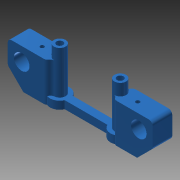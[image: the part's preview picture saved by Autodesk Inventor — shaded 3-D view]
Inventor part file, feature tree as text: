
AUTODESK INVENTOR PART (.ipt)
format: ipt  version: 2013 SP2 (Build 170200200, 200)  size: 180,736 bytes
history: native  units: mm
features: extrude x5, sketch x4, chamfer x1, fillet x1
ambient origin geometry x8: Origin, YZ Plane, XZ Plane, XY Plane, X Axis, Y Axis, Z Axis, Center Point
bodies: Solid1 (feature_tree)
feature tree (11):
  extrude  "Extrusion1"  Depth=6.0mm
  extrude  "Extrusion2"  Depth=10.0mm
  extrude  "Extrusion3"  Depth=4.0mm
  extrude  "Extrusion4"  Depth=20.0mm
  chamfer  "Chamfer1"  Distance=20.0mm
  fillet  "Fillet1"  Radius=8.0mm
  extrude  "Extrusion5"  Depth=8.0mm
  sketch  "Sketch2"  dims[d0=3.3mm d1=6.0mm]
  sketch  "Sketch3"  dims[d2=26.0mm d3=0.0mm d4=10.0mm]
  sketch  "Sketch4"  dims[d5=4.0mm d6=0.0mm d7=4.0mm]
  sketch  "Sketch5"  dims[d8=20.0mm d10=20.0mm d11=20.0mm d12=0.0mm d13=8.0mm d14=8.0mm d15=13.0mm d16=20.0mm d17=0.0mm d18=8.0mm d19=2.0mm d20=45.0deg d21=2.0mm d22=31.0mm d23=60.0mm d24=7.15mm d25=7.15mm d26=2.0mm d27=2.0mm d28=5.0mm d29=5.0mm d30=10.0mm d31=0.0mm]
